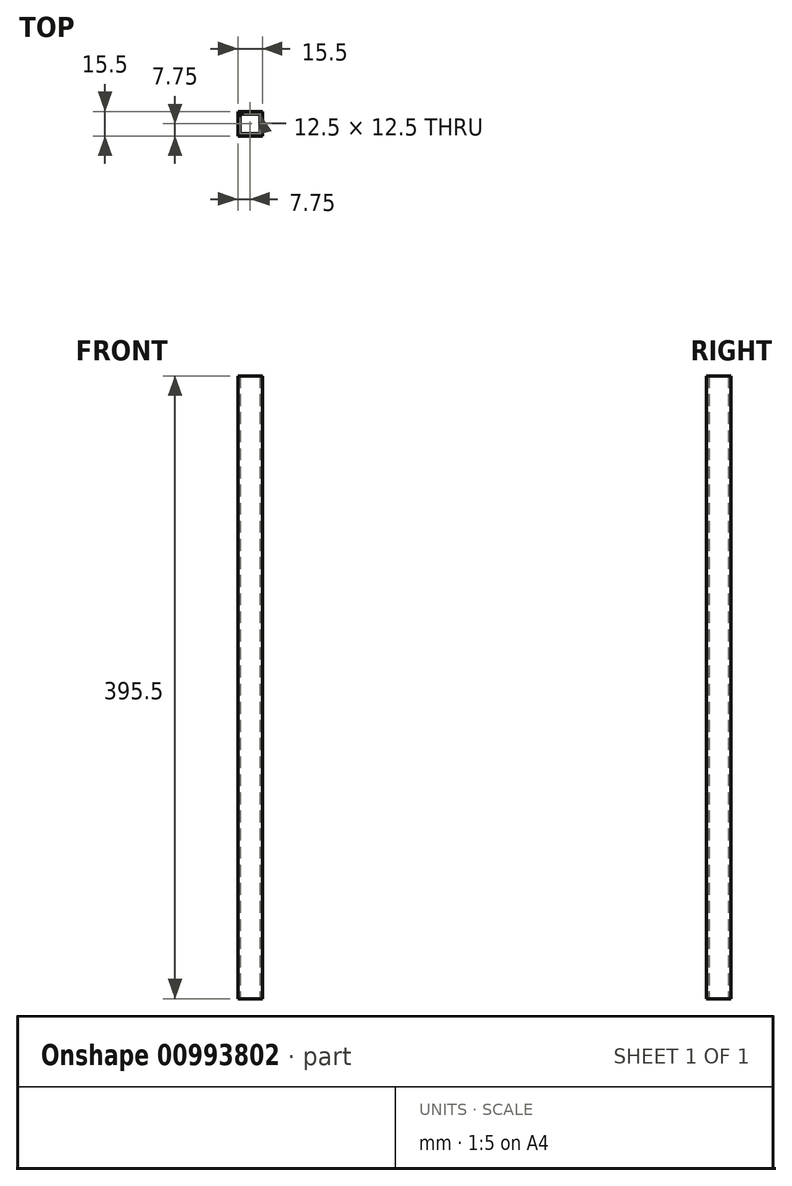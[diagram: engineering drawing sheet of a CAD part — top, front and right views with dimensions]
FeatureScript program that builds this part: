
annotation { "Feature Type Name" : "Feature", "Feature Type Description" : "" }
export const myFeature = defineFeature(function(context is Context, id is Id, definition is map)
    precondition{}
    {
        {
            var Q0;
            Q0=qCreatedBy(makeId("Top.planeOp"),FACE);
            var sketch = newSketch(context, id + "F0", { "sketchPlane" : qUnion([Q0])});
            skLineSegment(sketch, "E0.bottom", {"start": v(6.25, 6.25) * mm, "end": v(-6.25, 6.25) * mm});
            skLineSegment(sketch, "E0.top", {"start": v(6.25, -6.25) * mm, "end": v(-6.25, -6.25) * mm});
            skLineSegment(sketch, "E0.left", {"start": v(6.25, 6.25) * mm, "end": v(6.25, -6.25) * mm});
            skLineSegment(sketch, "E0.right", {"start": v(-6.25, 6.25) * mm, "end": v(-6.25, -6.25) * mm});
            skPoint(sketch, "E0.middle", {"position": v(0, 0) * mm});
            skLineSegment(sketch, "E1.bottom", {"start": v(7.75, 7.75) * mm, "end": v(-7.75, 7.75) * mm});
            skLineSegment(sketch, "E1.top", {"start": v(7.75, -7.75) * mm, "end": v(-7.75, -7.75) * mm});
            skLineSegment(sketch, "E1.left", {"start": v(7.75, 7.75) * mm, "end": v(7.75, -7.75) * mm});
            skLineSegment(sketch, "E1.right", {"start": v(-7.75, 7.75) * mm, "end": v(-7.75, -7.75) * mm});
            skSolve(sketch);
        }
        {
            var Q0;
            Q0=makeQuery(id+"F0.imprint","IMPRINT",FACE,{"disambiguationData":[TD([[makeQuery(id+"F0.imprint","IMPRINT",EDGE,{"derivedFrom":sQuery(id+"F0.wireOp",EDGE,"E0.bottom")}),-1.0]])]});
            extrude(context, id + "F1", {"entities" : qUnion([Q0]), "depth" : 395.5 * mm, "offsetDistance" : 25 * mm, "symmetric" : true});
        }
    });
